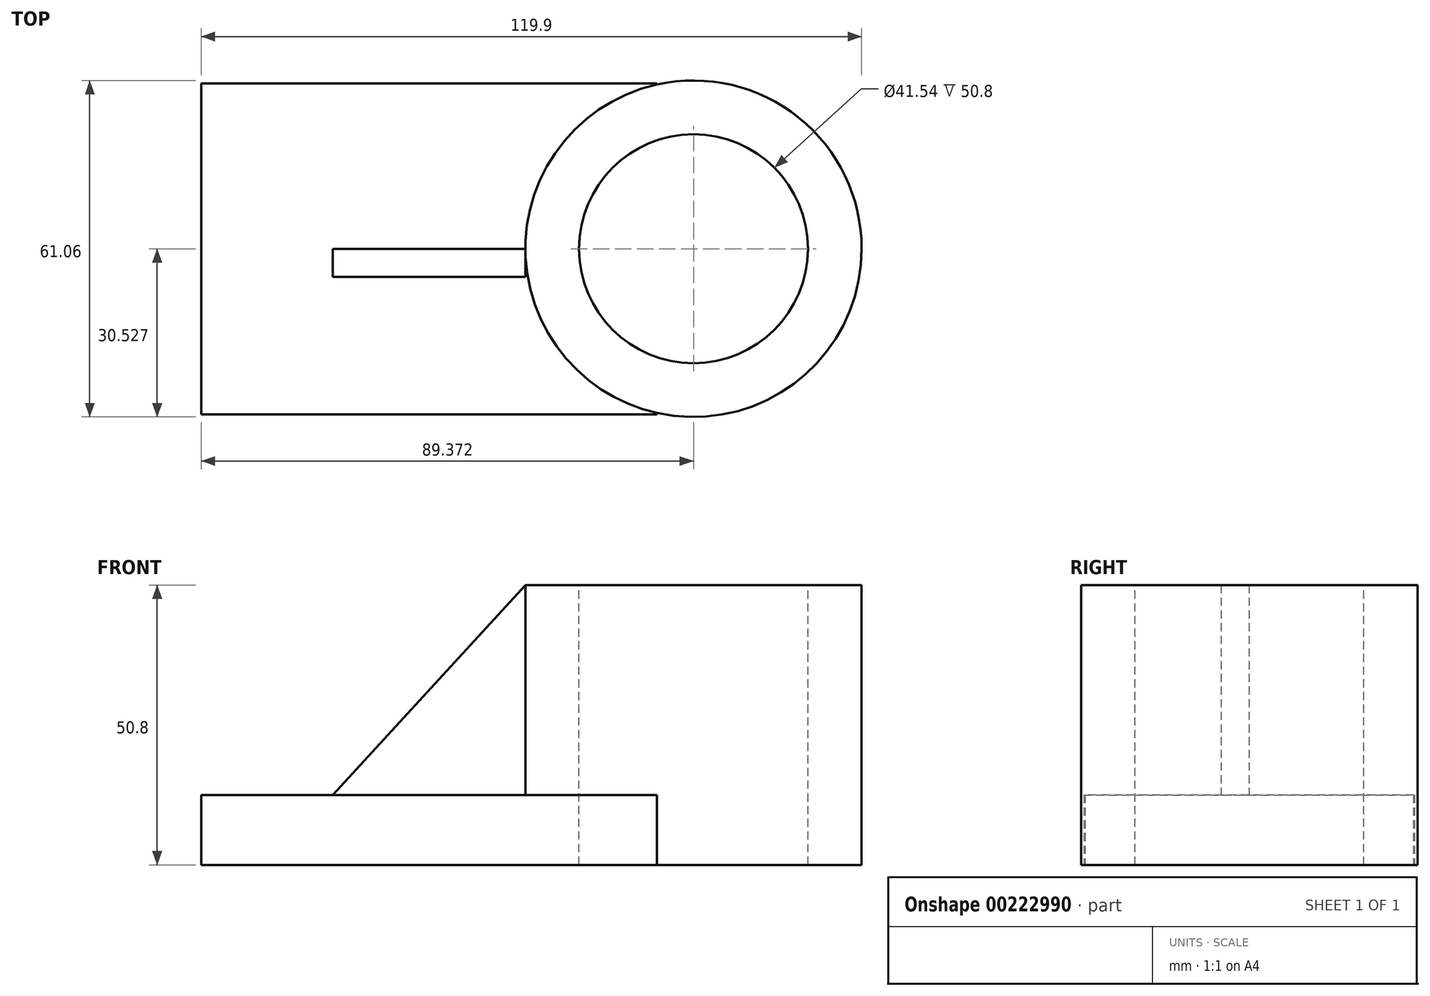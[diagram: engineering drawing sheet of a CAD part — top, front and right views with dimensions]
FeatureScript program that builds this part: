
annotation { "Feature Type Name" : "Feature", "Feature Type Description" : "" }
export const myFeature = defineFeature(function(context is Context, id is Id, definition is map)
    precondition{}
    {
        {
            var Q0;
            Q0=qCreatedBy(makeId("Top.planeOp"),FACE);
            var sketch = newSketch(context, id + "F0", { "sketchPlane" : qUnion([Q0])});
            skLineSegment(sketch, "E0.bottom", {"start": v(-41.38, -30.02) * mm, "end": v(41.38, -30.02) * mm});
            skLineSegment(sketch, "E0.top", {"start": v(-41.38, 30.02) * mm, "end": v(41.38, 30.02) * mm});
            skLineSegment(sketch, "E0.left", {"start": v(-41.38, -30.02) * mm, "end": v(-41.38, 30.02) * mm});
            skLineSegment(sketch, "E0.right", {"start": v(41.38, -30.02) * mm, "end": v(41.38, 30.02) * mm});
            skPoint(sketch, "E0.middle", {"position": v(0, 0) * mm});
            skSolve(sketch);
        }
        {
            var Q0;
            Q0 = qSketchRegion(id + "F0", true);
            extrude(context, id + "F1", {"entities" : qUnion([Q0]), "depth" : 12.7 * mm});
        }
        {
            var Q0;
            Q0=qCreatedBy(makeId("Top.planeOp"),FACE);
            var sketch = newSketch(context, id + "F2", { "sketchPlane" : qUnion([Q0])});
            skCircle(sketch, "E1", {"center": v(48, 0.03) * mm, "radius": 30.53 * mm});
            skPoint(sketch, "E1.first.point", {"position": v(41.14, 29.78) * mm});
            skPoint(sketch, "E1.second.point", {"position": v(41.38, -29.78) * mm});
            skPoint(sketch, "E1.third.point", {"position": v(17.46, 0) * mm});
            skSolve(sketch);
        }
        {
            var Q0;
            Q0 = qSketchRegion(id + "F2", true);
            extrude(context, id + "F3", {"entities" : qUnion([Q0]), "operationType" : NewBodyOperationType.ADD, "depth" : 50.8 * mm});
        }
        {
            var Q0;
            Q0=qCreatedBy(makeId("Front.planeOp"),FACE);
            var sketch = newSketch(context, id + "F4", { "sketchPlane" : qUnion([Q0])});
            skLineSegment(sketch, "E2", {"start": v(17.46, 12.7) * mm, "end": v(17.46, 50.8) * mm});
            skLineSegment(sketch, "E3.0", {"start": v(-41.38, 12.7) * mm, "end": v(41.38, 12.7) * mm});
            skLineSegment(sketch, "E4", {"start": v(17.46, 50.8) * mm, "end": v(-17.5, 12.7) * mm});
            skSolve(sketch);
        }
        {
            var Q0;
            Q0 = qSketchRegion(id + "F4", true);
            extrude(context, id + "F5", {"entities" : qUnion([Q0]), "operationType" : NewBodyOperationType.ADD, "depth" : 5.08 * mm});
        }
        {
            var Q0;
            Q0=makeQuery(id+"F3.opExtrude","CAP_FACE",FACE,{"disambiguationData":[OSD([sQuery(id+"F2.wireOp",EDGE,"E1")])],"isStart":false});
            var sketch = newSketch(context, id + "F6", { "sketchPlane" : qUnion([Q0])});
            skCircle(sketch, "E5", {"center": v(48, 0.03) * mm, "radius": 20.77 * mm});
            skSolve(sketch);
        }
        {
            var Q0;
            Q0 = qSketchRegion(id + "F6", true);
            extrude(context, id + "F7", {"entities" : qUnion([Q0]), "operationType" : NewBodyOperationType.REMOVE, "endBound" : BoundingType.THROUGH_ALL, "oppositeDirection" : true, "depth" : 25.4 * mm});
        }
    });
